FCSTD DOCUMENT  (FreeCAD 1.0R39109 (Git))
Label: SWITCH1_FOOTPRINT
License: All rights reserved
objects: Sketcher::SketchObject×1, PartDesign::Body×1
note: 3 computed .brp shape members not serialized (recipe doc carries the construction recipe); baked Part::Feature solids carry a one-line shape summary decoded from their .brp

FEATURE [Sketcher::SketchObject] Sketch
  ArcFitTolerance = 1e-06
  AttachmentSupport = -> [XY_Plane]
  FullyConstrained = true
  MakeInternals = false
  MapMode = 5
  sketch-geometry (18):
    g0: LineSegment StartX=-2.4 StartY=3.65 StartZ=0 EndX=-2.4 EndY=2.15 EndZ=0
    g1: LineSegment StartX=-2.4 StartY=2.15 StartZ=0 EndX=-1 EndY=2.15 EndZ=0
    g2: LineSegment StartX=-1 StartY=2.15 StartZ=0 EndX=-1 EndY=3.65 EndZ=0
    g3: LineSegment StartX=-1 StartY=3.65 StartZ=0 EndX=-2.4 EndY=3.65 EndZ=0
    g4: LineSegment StartX=1 StartY=3.65 StartZ=0 EndX=1 EndY=2.15 EndZ=0
    g5: LineSegment StartX=1 StartY=2.15 StartZ=0 EndX=2.4 EndY=2.15 EndZ=0
    g6: LineSegment StartX=2.4 StartY=2.15 StartZ=0 EndX=2.4 EndY=3.65 EndZ=0
    g7: LineSegment StartX=2.4 StartY=3.65 StartZ=0 EndX=1 EndY=3.65 EndZ=0
    g8: LineSegment StartX=-2.4 StartY=-2.15 StartZ=0 EndX=-2.4 EndY=-3.65 EndZ=0
    g9: LineSegment StartX=-2.4 StartY=-3.65 StartZ=0 EndX=-1 EndY=-3.65 EndZ=0
    g10: LineSegment StartX=-1 StartY=-3.65 StartZ=0 EndX=-1 EndY=-2.15 EndZ=0
    g11: LineSegment StartX=-1 StartY=-2.15 StartZ=0 EndX=-2.4 EndY=-2.15 EndZ=0
    g12: LineSegment StartX=1 StartY=-2.15 StartZ=0 EndX=1 EndY=-3.65 EndZ=0
    g13: LineSegment StartX=1 StartY=-3.65 StartZ=0 EndX=2.4 EndY=-3.65 EndZ=0
    g14: LineSegment StartX=2.4 StartY=-3.65 StartZ=0 EndX=2.4 EndY=-2.15 EndZ=0
    g15: LineSegment StartX=2.4 StartY=-2.15 StartZ=0 EndX=1 EndY=-2.15 EndZ=0
    g16: Circle CenterX=-1.5 CenterY=0 CenterZ=0 NormalX=0 NormalY=0 NormalZ=1 AngleXU=0 Radius=0.45
    g17: Circle CenterX=1.5 CenterY=0 CenterZ=0 NormalX=0 NormalY=0 NormalZ=1 AngleXU=0 Radius=0.45
  constraints (54):
    c: Coincident(g0,g1)
    c: Coincident(g1,g2)
    c: Coincident(g2,g3)
    c: Coincident(g3,g0)
    c: Vertical(g0)
    c: Vertical(g2)
    c: Horizontal(g1)
    c: Horizontal(g3)
    c: Coincident(g4,g5)
    c: Coincident(g5,g6)
    c: Coincident(g6,g7)
    c: Coincident(g7,g4)
    c: Vertical(g4)
    c: Vertical(g6)
    c: Horizontal(g5)
    c: Horizontal(g7)
    c: Coincident(g8,g9)
    c: Coincident(g9,g10)
    c: Coincident(g10,g11)
    c: Coincident(g11,g8)
    c: Vertical(g8)
    c: Vertical(g10)
    c: Horizontal(g9)
    c: Horizontal(g11)
    c: Coincident(g12,g13)
    c: Coincident(g13,g14)
    c: Coincident(g14,g15)
    c: Coincident(g15,g12)
    c: Vertical(g12)
    c: Vertical(g14)
    c: Horizontal(g13)
    c: Horizontal(g15)
    c: PointOnObject(g16,g-1)
    c: PointOnObject(g17,g-1)
    c: DistanceX(g16,g17) = 3
    c: Equal(g17,g16)
    c: Diameter(g17) = 0.9
    c: DistanceX(g16,g-1) = 1.5
    c: DistanceY(g13,g6) = 7.3
    c: DistanceY(g14,g5) = 4.3
    c: DistanceX(g10,g12) = 2
    c: DistanceX(g8,g13) = 4.8
    c: Equal(g14,g6)
    c: Equal(g6,g2)
    c: Equal(g2,g10)
    c: Equal(g11,g3)
    c: Equal(g3,g7)
    c: Equal(g7,g15)
    c: DistanceX(g-1,g12) = 1
    c: DistanceY(g-1,g4) = 2.15
    c: Horizontal(g2,g4)
    c: Horizontal(g12,g9)
    c: Vertical(g5,g14)
    c: Vertical(g0,g8)
FEATURE [PartDesign::Body] Body
  AllowCompound = false
  Group = -> [Sketch]
  Origin = -> Origin
